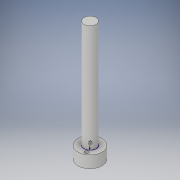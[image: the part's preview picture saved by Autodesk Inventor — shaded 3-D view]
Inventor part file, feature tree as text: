
AUTODESK INVENTOR PART (.ipt)
format: ipt  version: 2019 (Build 230136000, 136)  size: 128,512 bytes
history: native  units: mm
features: sketch x9, extrude x5, delete_face x3, hole x1
ambient origin geometry x8: Origin, YZ Plane, XZ Plane, XY Plane, X Axis, Y Axis, Z Axis, Center Point
bodies: Solid1 (feature_tree)
feature tree (18):
  sketch  "Sketch1"  dims[d0=20.0mm d1=180.0mm d2=0.0mm]
  extrude  "Extrusion1"  Depth=180.0mm TaperAngle=0.0deg
  extrude  "Extrusion2"  Depth=20.0mm TaperAngle=0.0deg
  sketch  "Sketch4"  dims[d8=20.0mm d9=6.0mm d10=4.0mm d11=2.0mm d12=90.0deg d13=8.0mm d14=20.594885mm d15=6.0mm]
  extrude  "Extrusion3"  Depth=20.0mm
  hole  "Hole1"  [1 undecoded]
  delete_face  "Delete Face1"
  delete_face  "Delete Face2"
  delete_face  "Delete Face3"
  sketch  "Sketch7"  dims[d21=40.0mm d22=0.0mm]
  extrude  "Extrusion4"  Depth=6.0mm
  extrude  "Extrusion5"  [1 undecoded]
  sketch  "Sketch2"  dims[d3=40.0mm d4=20.0mm d5=0.0mm]
  sketch  "Sketch3"  dims[d6=30.0mm d7=0.0mm]
  sketch  "Sketch5"  dims[d16=6.0mm d17=6.0mm]
  sketch  "Sketch6"  dims[d18=40.0mm d19=0.0mm d20=6.0mm]
  sketch  "Sketch8"
  sketch  "Sketch9"
note: 2 required parameter values undecoded (feature->parameter linkage not recoverable at this tier; creation-order binding heuristic only, values carry confidence <= 0.55)
